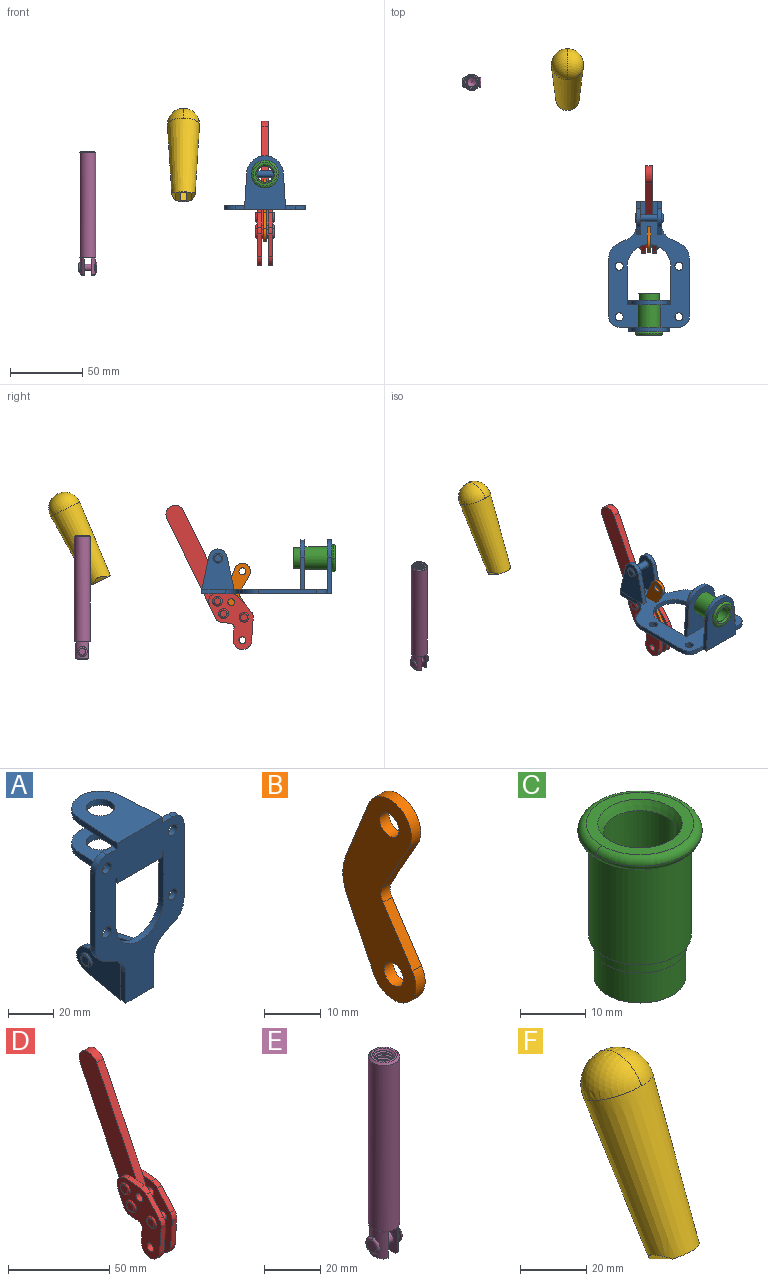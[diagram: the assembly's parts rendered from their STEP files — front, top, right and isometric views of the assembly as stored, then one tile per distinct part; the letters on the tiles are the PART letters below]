
ASSEMBLY  parts=6 mates=1
PART A: 55 faces, bbox 55.7x37.4x89.8 mm
  f0: torus R=2.41mm, axis (-1,0,0), area 15mm2, adj f11,f15,f25
  f1: torus R=2.41mm, axis (-1,0,0), area 15mm2, adj f10,f12,f22
  f2: cylinder r=2.78mm len=5.56mm, axis (0,-1,0), area 54.2mm2, adj f30,f54
  f3: cylinder r=14.99mm len=29.97mm, axis (0,-1,0), area 145.9mm2, adj f30,f49,f53,f54
  f4: cylinder r=2.78mm len=5.56mm, axis (0,-1,0), area 54.2mm2, adj f30,f54
  f5: cylinder r=2.78mm len=5.56mm, axis (0,-1,0), area 54.2mm2, adj f30,f54
  f6: cylinder r=2.78mm len=5.56mm, axis (0,-1,0), area 54.2mm2, adj f30,f54
  f7: cylinder r=6.35mm len=12.7mm, axis (0,0,1), area 123.6mm2, adj f27,f51
  f8: cylinder r=6.35mm len=12.7mm, axis (0,0,-1), area 124.7mm2, adj f21,f35
  f9: cylinder r=2.41mm len=11.18mm, axis (-1,0,0), area 169.4mm2, adj f16,f19
  f10: plane 4.83x4.83mm, normal (1,0,0), area 18.3mm2, adj f1,f12
  f11: plane 4.83x4.83mm, normal (-1,0,0), area 18.3mm2, adj f0,f15
  f12: torus R=2.41mm, axis (-1,0,0), area 15mm2, adj f1,f10,f22
  f13: cylinder r=6.35mm len=12.41mm, axis (1,0,0), area 53.4mm2, adj f18,f19,f22,f23
  f14: cylinder r=6.35mm len=12.41mm, axis (-1,0,0), area 53.4mm2, adj f16,f17,f24,f25
  f15: torus R=2.41mm, axis (-1,0,0), area 15mm2, adj f0,f11,f25
  f16: plane 27.86x22.35mm, normal (1,0,0), area 425.4mm2, adj f9,f14,f17,f24,f30
  f17: plane 22.86x4.97mm, normal (0,0.21,0.98), area 72.5mm2, adj f14,f16,f25,f30
  f18: plane 22.86x4.97mm, normal (0,0.21,0.98), area 72.5mm2, adj f13,f19,f22,f30
  f19: plane 27.86x22.35mm, normal (-1,0,0), area 425.4mm2, adj f9,f13,f18,f23,f30
  f20: cylinder r=12.7mm len=25.35mm, axis (0,0,-1), area 119.8mm2, adj f21,f34,f35,f36
  f21: plane 34.21x28.07mm, normal (0,0,-1), area 702.4mm2, adj f8,f20,f30,f34,f36
  f22: plane 27.96x22.45mm, normal (1,0,0), area 407.2mm2, adj f1,f12,f13,f18,f23,f30,f42,f43
  f23: plane 22.86x4.97mm, normal (0,0.21,-0.98), area 72.5mm2, adj f13,f19,f22,f44
  f24: plane 22.86x4.97mm, normal (0,0.21,-0.98), area 72.5mm2, adj f14,f16,f25,f44
  f25: plane 27.86x22.35mm, normal (-1,0,0), area 407.1mm2, adj f0,f14,f15,f17,f24,f30,f45,f46
  f26: plane 3.1x0.95mm, normal (0,0,-1), area 2.7mm2, adj f30,f49,f50,f54
  f27: plane 34.21x28.07mm, normal (0,0,1), area 702.4mm2, adj f7,f28,f30,f50,f52
  f28: cylinder r=12.7mm len=25.35mm, axis (0,0,1), area 118.8mm2, adj f27,f50,f51,f52
  f29: plane 3.1x0.95mm, normal (0,0,-1), area 2.7mm2, adj f30,f52,f53,f54
  f30: plane 86.54x55.63mm, normal (0,1,0), area 2362.9mm2, adj f2,f3,f4,f5,f6,f16,f17,f18
  f31: plane 40.56x3.1mm, normal (-1,0,0), area 125.7mm2, adj f30,f32,f48,f54
  f32: cylinder r=7.11mm len=7.11mm, axis (0,-1,0), area 34.6mm2, adj f30,f31,f33,f54
  f33: plane 6.67x3.1mm, normal (0,0,1), area 20.4mm2, adj f30,f32,f34,f54
  f34: plane 25.39x3.13mm, normal (-1,0.06,0), area 79.5mm2, adj f20,f21,f33,f35,f54
  f35: plane 37.31x28.45mm, normal (0,0,1), area 789.9mm2, adj f8,f20,f34,f36,f54
  f36: plane 25.39x3.13mm, normal (1,0.06,0), area 79.5mm2, adj f20,f21,f35,f37,f54
  f37: plane 6.67x3.1mm, normal (0,0,1), area 20.4mm2, adj f30,f36,f38,f54
  f38: cylinder r=7.11mm len=7.11mm, axis (0,-1,0), area 34.6mm2, adj f30,f37,f39,f54
  f39: plane 40.56x3.1mm, normal (1,0,0), area 125.7mm2, adj f30,f38,f40,f54
  f40: cylinder r=11.18mm len=10.16mm, axis (0,-1,0), area 39.5mm2, adj f30,f39,f41,f54
  f41: plane 6.09x3.1mm, normal (0.42,0,-0.91), area 20.8mm2, adj f30,f40,f42,f54
  f42: cylinder r=11.18mm len=9.41mm, axis (0,-1,0), area 37.2mm2, adj f22,f30,f41,f43,f54
  f43: plane 16.5x3.1mm, normal (1,0,0), area 51.1mm2, adj f22,f42,f44,f54
  f44: plane 17.37x3.1mm, normal (0,0,-1), area 53.8mm2, adj f23,f24,f30,f43,f45,f54
  f45: plane 16.5x3.1mm, normal (-1,0,0), area 51.1mm2, adj f25,f44,f46,f54
  f46: cylinder r=11.18mm len=9.41mm, axis (0,-1,0), area 37.2mm2, adj f25,f30,f45,f47,f54
  f47: plane 6.09x3.1mm, normal (-0.42,0,-0.91), area 20.8mm2, adj f30,f46,f48,f54
  f48: cylinder r=11.18mm len=10.16mm, axis (0,-1,0), area 39.5mm2, adj f30,f31,f47,f54
  f49: plane 26.54x3.1mm, normal (-1,0,0), area 82.3mm2, adj f3,f26,f30,f54
  f50: plane 25.39x3.1mm, normal (1,0.06,0), area 78.8mm2, adj f26,f27,f28,f51,f54
  f51: plane 37.31x28.45mm, normal (0,0,-1), area 789.9mm2, adj f7,f28,f50,f52,f54
  f52: plane 25.39x3.1mm, normal (-1,0.06,0), area 78.8mm2, adj f27,f28,f29,f51,f54
  f53: plane 26.54x3.1mm, normal (1,0,0), area 82.3mm2, adj f3,f29,f30,f54
  f54: plane 89.66x55.63mm, normal (0,-1,0), area 2678.5mm2, adj f2,f3,f4,f5,f6,f26,f29,f31
PART B: 12 faces, bbox 2.3x18.2x42.8 mm
  f0: cylinder r=2.4mm len=4.8mm, axis (1,0,0), area 34.9mm2, adj f4,f11
  f1: cylinder r=10.41mm len=8.47mm, axis (1,0,0), area 20.2mm2, adj f4,f9,f10,f11
  f2: cylinder r=3.05mm len=3.16mm, axis (1,0,0), area 7.7mm2, adj f4,f6,f7,f11
  f3: cylinder r=2.4mm len=4.8mm, axis (1,0,0), area 34.9mm2, adj f4,f11
  f4: plane 42.81x18.23mm, normal (-1,0,0), area 414.1mm2, adj f0,f1,f2,f3,f5,f6,f7,f8
  f5: cylinder r=5.54mm len=10.67mm, axis (1,0,0), area 41.8mm2, adj f4,f6,f10,f11
  f6: plane 11.66x6.53mm, normal (0,-0.87,-0.49), area 30.9mm2, adj f2,f4,f5,f11
  f7: plane 11.17x7.33mm, normal (0,-0.84,0.55), area 30.9mm2, adj f2,f4,f8,f11
  f8: cylinder r=5.54mm len=10.51mm, axis (1,0,0), area 41.8mm2, adj f4,f7,f9,f11
  f9: plane 13.67x6.67mm, normal (0,0.9,-0.44), area 35.1mm2, adj f1,f4,f8,f11
  f10: plane 14.1x5.7mm, normal (0,0.93,0.37), area 35.1mm2, adj f1,f4,f5,f11
  f11: plane 42.81x18.23mm, normal (1,0,0), area 414.1mm2, adj f0,f1,f2,f3,f5,f6,f7,f8
PART C: 15 faces, bbox 20.6x20.6x28.7 mm
  f0: torus R=8.26mm, axis (0,0,1), area 56.8mm2, adj f1,f10,f12
  f1: torus R=8.26mm, axis (0,0,1), area 56.8mm2, adj f0,f6,f13
  f2: cylinder r=5.59mm len=25.91mm, axis (0,0,1), area 909.6mm2, adj f3,f4
  f3: cone r=6.86mm half-angle=45deg, axis (0,0,-1), area 70.2mm2, adj f2,f14
  f4: cone r=6.47mm half-angle=30deg, axis (0,0,1), area 66.7mm2, adj f2,f13
  f5: cylinder r=7.04mm len=14.07mm, axis (0,0,1), area 252.6mm2, adj f11,f14
  f6: torus R=8.26mm, axis (0,0,1), area 56.8mm2, adj f1,f12,f13
  f7: cylinder r=7.16mm len=14.33mm, axis (0,0,1), area 91.5mm2, adj f9,f11
  f8: cylinder r=7.86mm len=18.42mm, axis (0,0,1), area 909.6mm2, adj f9,f10
  f9: plane 15.72x15.72mm, normal (0,0,-1), area 33mm2, adj f7,f8
  f10: plane 16.51x16.51mm, normal (0,0,-1), area 19.9mm2, adj f0,f8,f12
  f11: plane 14.33x14.33mm, normal (0,0,-1), area 5.7mm2, adj f5,f7
  f12: torus R=8.26mm, axis (0,0,1), area 56.8mm2, adj f0,f6,f10
  f13: plane 16.51x16.51mm, normal (0,0,1), area 82.7mm2, adj f1,f4,f6
  f14: plane 14.07x14.07mm, normal (0,0,-1), area 7.8mm2, adj f3,f5
PART D: 59 faces, bbox 12.9x60.2x99.6 mm
  f0: torus R=2.39mm, axis (-1,0,0), area 14.9mm2, adj f20,f43,f51
  f1: torus R=2.39mm, axis (-1,0,0), area 14.9mm2, adj f19,f42,f51
  f2: torus R=2.39mm, axis (-1,0,0), area 14.9mm2, adj f18,f35,f51
  f3: torus R=2.39mm, axis (-1,0,0), area 14.9mm2, adj f14,f17,f23
  f4: torus R=2.39mm, axis (-1,0,0), area 14.9mm2, adj f13,f16,f23
  f5: torus R=2.39mm, axis (-1,0,0), area 14.9mm2, adj f12,f15,f23
  f6: cylinder r=2.39mm len=4.78mm, axis (1,0,0), area 46.5mm2, adj f48,f50,f51
  f7: cylinder r=2.39mm len=4.78mm, axis (1,0,0), area 46.5mm2, adj f50,f51
  f8: cylinder r=6.35mm len=12.68mm, axis (1,0,0), area 61.8mm2, adj f38,f39,f50,f51
  f9: cylinder r=2.39mm len=4.78mm, axis (-1,0,0), area 70.5mm2, adj f46,f50
  f10: cylinder r=2.39mm len=4.78mm, axis (-1,0,0), area 46.5mm2, adj f23,f45,f46
  f11: cylinder r=2.39mm len=4.78mm, axis (-1,0,0), area 46.5mm2, adj f23,f46
  f12: plane 4.78x4.78mm, normal (1,0,0), area 17.9mm2, adj f5,f15
  f13: plane 4.78x4.78mm, normal (1,0,0), area 17.9mm2, adj f4,f16
  f14: plane 4.78x4.78mm, normal (1,0,0), area 17.9mm2, adj f3,f17
  f15: torus R=2.39mm, axis (-1,0,0), area 14.9mm2, adj f5,f12,f23
  f16: torus R=2.39mm, axis (-1,0,0), area 14.9mm2, adj f4,f13,f23
  f17: torus R=2.39mm, axis (-1,0,0), area 14.9mm2, adj f3,f14,f23
  f18: plane 4.78x4.78mm, normal (-1,0,0), area 17.9mm2, adj f2,f35
  f19: plane 4.78x4.78mm, normal (-1,0,0), area 17.9mm2, adj f1,f42
  f20: plane 4.78x4.78mm, normal (-1,0,0), area 17.9mm2, adj f0,f43
  f21: plane 2.26x0.2mm, normal (1,0,0), area 0.2mm2, adj f31,f44
  f22: plane 2.26x0.2mm, normal (-1,0,0), area 0.2mm2, adj f41,f44
  f23: plane 39.37x30.77mm, normal (1,0,0), area 565.5mm2, adj f3,f4,f5,f10,f11,f15,f16,f17
  f24: cylinder r=6.1mm len=4.15mm, axis (-1,0,0), area 14.7mm2, adj f23,f25,f32,f46
  f25: plane 10.25x9.01mm, normal (0,-0.75,0.66), area 42.3mm2, adj f23,f24,f26,f46
  f26: cylinder r=6.35mm len=4.64mm, axis (-1,0,0), area 15.6mm2, adj f23,f25,f27,f46
  f27: plane 15.84x3.1mm, normal (0,-1,-0.07), area 49.2mm2, adj f23,f26,f28,f46
  f28: cylinder r=6.35mm len=12.68mm, axis (-1,0,0), area 61.8mm2, adj f23,f27,f29,f46
  f29: plane 8.11x3.1mm, normal (0,1,0.07), area 25.2mm2, adj f23,f28,f30,f46
  f30: cylinder r=3.05mm len=3.25mm, axis (-1,0,0), area 14.8mm2, adj f23,f29,f31,f46
  f31: plane 5.99x3.1mm, normal (0,0.07,-1), area 18.6mm2, adj f21,f23,f30,f44,f46
  f32: plane 9.5x3.1mm, normal (0,-0.07,1), area 29.5mm2, adj f23,f24,f33,f46,f47
  f33: cylinder r=6.1mm len=8.63mm, axis (-1,0,0), area 39.1mm2, adj f23,f32,f34,f47
  f34: plane 8.65x3.96mm, normal (0,0.91,-0.42), area 29.5mm2, adj f23,f33,f44,f47
  f35: torus R=2.39mm, axis (-1,0,0), area 14.9mm2, adj f2,f18,f51
  f36: plane 10.25x9.01mm, normal (0,-0.75,0.66), area 42.3mm2, adj f37,f49,f50,f51
  f37: cylinder r=6.35mm len=4.64mm, axis (1,0,0), area 15.6mm2, adj f36,f38,f50,f51
  f38: plane 15.84x3.1mm, normal (0,-1,-0.07), area 49.2mm2, adj f8,f37,f50,f51
  f39: plane 8.11x3.1mm, normal (0,1,0.07), area 25.2mm2, adj f8,f40,f50,f51
  f40: cylinder r=3.05mm len=3.25mm, axis (1,0,0), area 14.8mm2, adj f39,f41,f50,f51
  f41: plane 5.99x3.1mm, normal (0,0.07,-1), area 18.6mm2, adj f22,f40,f44,f50,f51
  f42: torus R=2.39mm, axis (-1,0,0), area 14.9mm2, adj f1,f19,f51
  f43: torus R=2.39mm, axis (-1,0,0), area 14.9mm2, adj f0,f20,f51
  f44: cylinder r=6.35mm len=12.12mm, axis (-1,0,0), area 128.9mm2, adj f21,f22,f23,f31,f34,f41,f46,f47
  f45: plane 2.65x1.35mm, normal (1,0,0), area 1mm2, adj f10,f55
  f46: plane 39.08x20.42mm, normal (-1,0,0), area 412.5mm2, adj f9,f10,f11,f24,f25,f26,f27,f28
  f47: plane 77.62x39.82mm, normal (1,0,0), area 850mm2, adj f32,f33,f34,f44,f53,f54,f55
  f48: plane 2.65x1.35mm, normal (-1,0,0), area 1mm2, adj f6,f55
  f49: cylinder r=6.1mm len=4.15mm, axis (1,0,0), area 14.7mm2, adj f36,f50,f51,f56
  f50: plane 39.08x20.42mm, normal (1,0,0), area 412.5mm2, adj f6,f7,f8,f9,f36,f37,f38,f39
  f51: plane 39.37x30.77mm, normal (-1,0,0), area 565.5mm2, adj f0,f1,f2,f6,f7,f8,f35,f36
  f52: plane 8.65x3.96mm, normal (0,0.91,-0.42), area 29.5mm2, adj f44,f51,f57,f58
  f53: plane 68.49x33.4mm, normal (0,0.9,-0.44), area 358.1mm2, adj f44,f47,f54,f58
  f54: cylinder r=6.35mm len=12.06mm, axis (1,0,0), area 93.7mm2, adj f47,f53,f55,f58
  f55: plane 68.49x33.4mm, normal (0,-0.9,0.44), area 358.1mm2, adj f44,f45,f46,f47,f48,f50,f54,f58
  f56: plane 9.5x3.1mm, normal (0,-0.07,1), area 29.5mm2, adj f49,f50,f51,f57,f58
  f57: cylinder r=6.1mm len=8.63mm, axis (1,0,0), area 39.1mm2, adj f51,f52,f56,f58
  f58: plane 77.62x39.82mm, normal (-1,0,0), area 850mm2, adj f44,f52,f53,f54,f55,f56,f57
PART E: 48 faces, bbox 12.6x11.1x86.1 mm
  f0: torus R=2.41mm, axis (-1,0,0), area 15mm2, adj f30,f32,f34
  f1: torus R=2.41mm, axis (-1,0,0), area 15mm2, adj f29,f31,f33
  f2: cylinder r=5.54mm len=72.39mm, axis (0,0,1), area 2518.5mm2, adj f3,f4,f42,f43
  f3: cone r=5.54mm half-angle=45deg, axis (0,0,1), area 7.6mm2, adj f2,f5,f41
  f4: cone r=5.54mm half-angle=45deg, axis (0,0,-1), area 34.9mm2, adj f2,f39
  f5: cylinder r=5.08mm len=11.48mm, axis (0,0,1), area 108.3mm2, adj f3,f7,f8,f41
  f6: cylinder r=2.41mm len=4.83mm, axis (-1,0,0), area 71.2mm2, adj f40,f41
  f7: cylinder r=2.41mm len=4.83mm, axis (-1,0,0), area 7.6mm2, adj f5,f34
  f8: cone r=5.08mm half-angle=45deg, axis (0,0,1), area 10.6mm2, adj f5,f37,f41
  f9: cone r=3.98mm half-angle=45deg, axis (0,0,1), area 17.6mm2, adj f27,f39,f45,f46,f47
  f10: cylinder r=2.41mm len=4.83mm, axis (-1,0,0), area 7.6mm2, adj f33,f38
  f11: cylinder r=3.2mm len=6.4mm, axis (0,0,1), area 78.4mm2, adj f12,f28,f44,f45,f47
  f12: cylinder r=3.2mm len=6.4mm, axis (0,0,1), area 10.5mm2, adj f11,f13,f45,f47
  f13: cylinder r=3.2mm len=6.4mm, axis (0,0,1), area 10.5mm2, adj f12,f14,f45,f47
  f14: cylinder r=3.2mm len=6.4mm, axis (0,0,1), area 10.5mm2, adj f13,f15,f45,f47
  f15: cylinder r=3.2mm len=6.4mm, axis (0,0,1), area 10.5mm2, adj f14,f16,f45,f47
  f16: cylinder r=3.2mm len=6.4mm, axis (0,0,1), area 10.5mm2, adj f15,f17,f45,f47
  f17: cylinder r=3.2mm len=6.4mm, axis (0,0,1), area 10.5mm2, adj f16,f18,f45,f47
  f18: cylinder r=3.2mm len=6.4mm, axis (0,0,1), area 10.5mm2, adj f17,f19,f45,f47
  f19: cylinder r=3.2mm len=6.4mm, axis (0,0,1), area 10.5mm2, adj f18,f20,f45,f47
  f20: cylinder r=3.2mm len=6.4mm, axis (0,0,1), area 10.5mm2, adj f19,f21,f45,f47
  f21: cylinder r=3.2mm len=6.4mm, axis (0,0,1), area 10.5mm2, adj f20,f22,f45,f47
  f22: cylinder r=3.2mm len=6.4mm, axis (0,0,1), area 10.5mm2, adj f21,f23,f45,f47
  f23: cylinder r=3.2mm len=6.4mm, axis (0,0,1), area 10.5mm2, adj f22,f24,f45,f47
  f24: cylinder r=3.2mm len=6.4mm, axis (0,0,1), area 10.5mm2, adj f23,f25,f45,f47
  f25: cylinder r=3.2mm len=6.4mm, axis (0,0,1), area 10.5mm2, adj f24,f26,f45,f47
  f26: cylinder r=3.2mm len=6.4mm, axis (0,0,1), area 10.5mm2, adj f25,f27,f45,f47
  f27: cylinder r=3.2mm len=6.4mm, axis (0,0,1), area 7.4mm2, adj f9,f26,f45,f47
  f28: cone r=3.2mm half-angle=60deg, axis (0,0,1), area 37.2mm2, adj f11
  f29: plane 4.83x4.83mm, normal (-1,0,0), area 18.3mm2, adj f1,f31
  f30: plane 4.83x4.83mm, normal (1,0,0), area 18.3mm2, adj f0,f32
  f31: torus R=2.41mm, axis (-1,0,0), area 15mm2, adj f1,f29,f33
  f32: torus R=2.41mm, axis (-1,0,0), area 15mm2, adj f0,f30,f34
  f33: plane 6.83x6.83mm, normal (1,0,0), area 18.3mm2, adj f1,f10,f31
  f34: plane 6.83x6.83mm, normal (-1,0,0), area 18.3mm2, adj f0,f7,f32
  f35: cone r=5.08mm half-angle=45deg, axis (0,0,1), area 10.6mm2, adj f36,f38,f40
  f36: plane 7.25x1.97mm, normal (0,0,-1), area 10mm2, adj f35,f40
  f37: plane 7.25x1.97mm, normal (0,0,-1), area 10mm2, adj f8,f41
  f38: cylinder r=5.08mm len=11.48mm, axis (0,0,1), area 108.3mm2, adj f10,f35,f40,f42
  f39: plane 9.55x9.55mm, normal (0,0,1), area 22mm2, adj f4,f9
  f40: plane 12.76x10.09mm, normal (1,0,0), area 95.7mm2, adj f6,f35,f36,f38,f42,f43
  f41: plane 12.76x10.09mm, normal (-1,0,0), area 95.7mm2, adj f3,f5,f6,f8,f37,f43
  f42: cone r=5.54mm half-angle=45deg, axis (0,0,1), area 7.6mm2, adj f2,f38,f40
  f43: plane 11.07x4.7mm, normal (0,0,-1), area 50.4mm2, adj f2,f40,f41
  f44: plane 0.89x0.62mm, normal (-1,0,0), area 0.3mm2, adj f11,f45,f46,f47
  f45: bspline ~24.8x7.63mm, area 266.6mm2, adj f9,f11,f12,f13,f14,f15,f16,f17
  f46: bspline ~24.87x7.63mm, area 73.6mm2, adj f9,f44,f45,f47
  f47: bspline ~24.98x7.63mm, area 272.5mm2, adj f9,f11,f12,f13,f14,f15,f16,f17
PART F: 11 faces, bbox 22.3x42.6x64.5 mm
  f0: sphere r=11.13mm, area 411.4mm2, adj f1,f8
  f1: cone r=11.11mm half-angle=3.3deg, axis (0,0.44,0.9), area 3251.8mm2, adj f0,f7,f8,f9,f10
  f2: cylinder r=6.16mm len=11.7mm, axis (1,0,0), area 89.5mm2, adj f3,f4,f5,f6
  f3: plane 60.23x36.75mm, normal (-1,0,0), area 763.6mm2, adj f2,f4,f6,f10
  f4: plane 51.37x25.05mm, normal (0,0.9,-0.44), area 264.2mm2, adj f2,f3,f5,f10
  f5: plane 60.23x36.75mm, normal (1,0,0), area 763.6mm2, adj f2,f4,f6,f10
  f6: plane 51.37x25.05mm, normal (0,-0.9,0.44), area 264.2mm2, adj f2,f3,f5,f10
  f7: plane 9.95x5.95mm, normal (0.71,-0.31,-0.64), area 25.8mm2, adj f1,f10
  f8: sphere r=11.13mm, area 411.4mm2, adj f0,f1
  f9: plane 9.95x5.95mm, normal (-0.71,-0.31,-0.64), area 25.8mm2, adj f1,f10
  f10: plane 14.27x11.38mm, normal (0,-0.44,-0.9), area 106.7mm2, adj f1,f3,f4,f5,f6,f7,f9
PLACE A rot(axis=(1,0,0),90deg) t=(0,9.43,0)mm fixed
PLACE B at identity
PLACE C rot(axis=(1,0,0),90deg) t=(0,9.43,0)mm
PLACE D at identity
PLACE E t=(-122.41,110.55,-55.4)mm
PLACE F t=(-56.34,76.89,5.61)mm
MATE fastened A.f7 <-> C.f2  axis (0,-1,0) through (0,-36.96,24.61)mm
